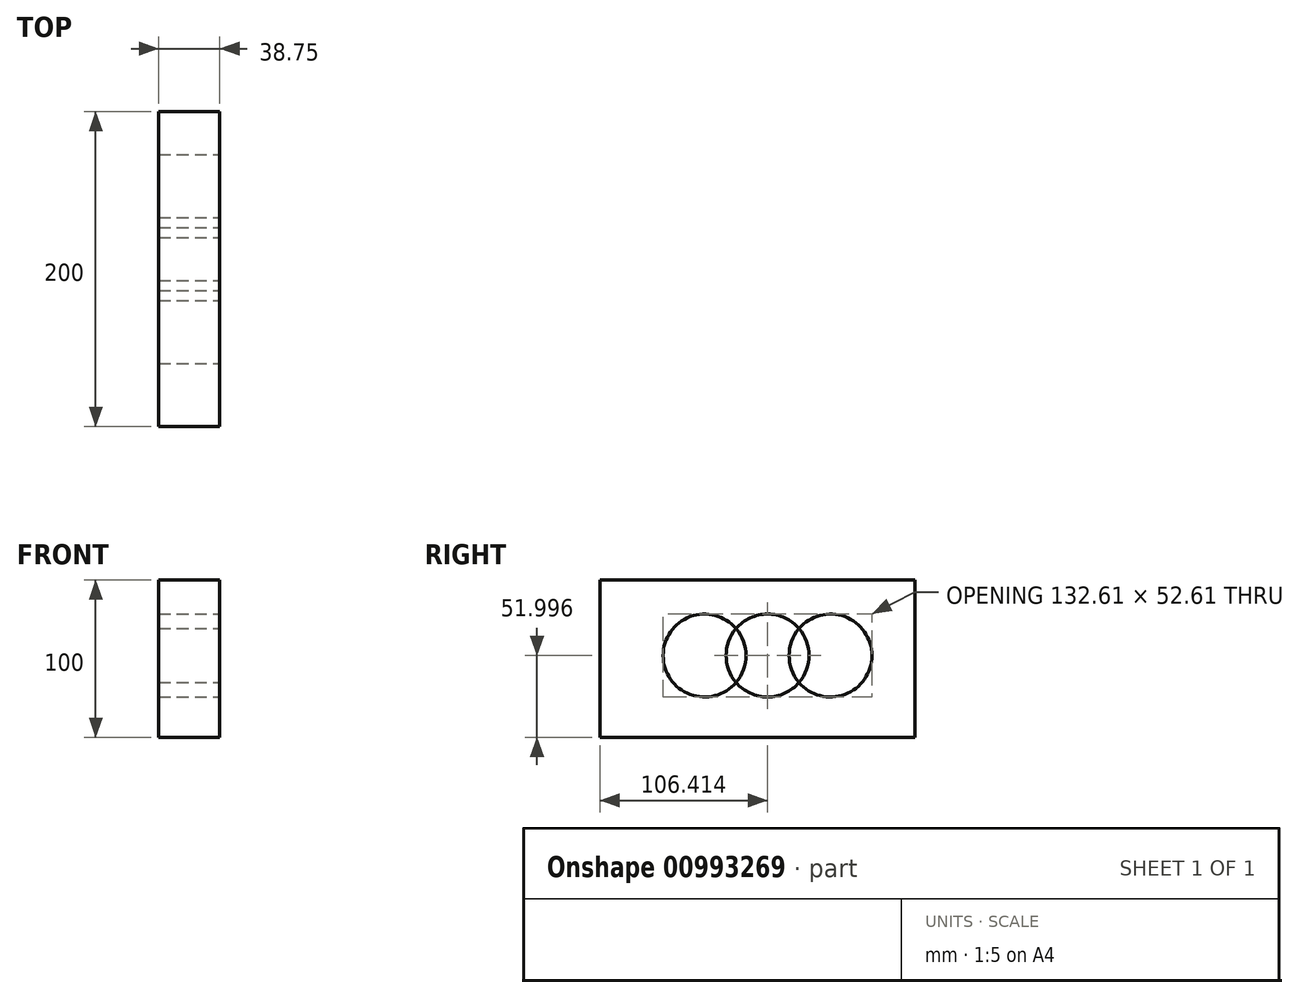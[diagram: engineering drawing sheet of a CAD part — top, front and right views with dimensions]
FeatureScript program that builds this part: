
annotation { "Feature Type Name" : "Feature", "Feature Type Description" : "" }
export const myFeature = defineFeature(function(context is Context, id is Id, definition is map)
    precondition{}
    {
        {
            var Q0;
            Q0=qCreatedBy(makeId("Top.planeOp"),FACE);
            var sketch = newSketch(context, id + "F0", { "sketchPlane" : qUnion([Q0])});
            skLineSegment(sketch, "E0", {"start": v(-54.4, 379.86) * mm, "end": v(-54.4, 179.86) * mm});
            skLineSegment(sketch, "E1", {"start": v(-54.4, 379.86) * mm, "end": v(-93.15, 379.86) * mm});
            skLineSegment(sketch, "E2", {"start": v(-93.15, 379.86) * mm, "end": v(-93.15, 179.86) * mm});
            skLineSegment(sketch, "E3", {"start": v(-93.15, 179.86) * mm, "end": v(-54.4, 179.86) * mm});
            skSolve(sketch);
        }
        {
            var Q0;
            Q0=makeQuery(id+"F0.imprint","IMPRINT",FACE,{"disambiguationData":[TD([[makeQuery(id+"F0.imprint","IMPRINT",EDGE,{"derivedFrom":sQuery(id+"F0.wireOp",EDGE,"E0")}),-1.0]])]});
            extrude(context, id + "F1", {"entities" : qUnion([Q0]), "depth" : 100 * mm, "offsetDistance" : 25 * mm});
        }
        {
            var Q0;
            Q0=makeQuery(id+"F1.opExtrude","SWEPT_FACE",FACE,{"disambiguationData":[OSD([sQuery(id+"F0.wireOp",EDGE,"E0")])]});
            var sketch = newSketch(context, id + "F2", { "sketchPlane" : qUnion([Q0])});
            skCircle(sketch, "E4", {"center": v(246.27, 52) * mm, "radius": 26.3 * mm});
            skCircle(sketch, "E5.1.0.0", {"center": v(286.27, 52) * mm, "radius": 26.3 * mm});
            skCircle(sketch, "E5.2.0.0", {"center": v(326.27, 52) * mm, "radius": 26.3 * mm});
            skLineSegment(sketch, "E5.direction1", {"start": v(246.27, 52) * mm, "end": v(286.27, 52) * mm, "construction": true});
            skSolve(sketch);
        }
        {
            var Q0;
            {var subQ0=sQuery(id+"F2.wireOp",EDGE,"E5.1.0.0");var subQ1=sQuery(id+"F2.wireOp",EDGE,"E4");var subQ2=makeQuery(id+"F2.imprint","INTERSECT",VERTEX,{"disambiguationData":[OD(0.0)],"derivedFrom":[subQ1,subQ0]});Q0=makeQuery(id+"F2.imprint","IMPRINT",FACE,{"disambiguationData":[TD([[makeQuery(id+"F2.imprint","IMPRINT",EDGE,{"disambiguationData":[TD([[subQ2,-1.0]])],"derivedFrom":subQ1}),1.0]])]});}
            var Q1;
            {var subQ0=sQuery(id+"F2.wireOp",EDGE,"E5.1.0.0");var subQ1=sQuery(id+"F2.wireOp",EDGE,"E4");var subQ2=makeQuery(id+"F2.imprint","INTERSECT",VERTEX,{"disambiguationData":[OD(0.0)],"derivedFrom":[subQ1,subQ0]});Q1=makeQuery(id+"F2.imprint","IMPRINT",FACE,{"disambiguationData":[TD([[makeQuery(id+"F2.imprint","IMPRINT",EDGE,{"disambiguationData":[TD([[subQ2,1.0]])],"derivedFrom":subQ1}),-1.0]])]});}
            var Q2;
            {var subQ0=sQuery(id+"F2.wireOp",EDGE,"E5.2.0.0");var subQ1=sQuery(id+"F2.wireOp",EDGE,"E5.1.0.0");var subQ2=makeQuery(id+"F2.imprint","INTERSECT",VERTEX,{"disambiguationData":[OD(0.0)],"derivedFrom":[subQ1,subQ0]});Q2=makeQuery(id+"F2.imprint","IMPRINT",FACE,{"disambiguationData":[TD([[makeQuery(id+"F2.imprint","IMPRINT",EDGE,{"disambiguationData":[TD([[subQ2,1.0]])],"derivedFrom":subQ1}),-1.0]])]});}
            extrude(context, id + "F3", {"entities" : qUnion([Q0, Q1, Q2]), "operationType" : NewBodyOperationType.REMOVE, "oppositeDirection" : true, "depth" : 200 * mm, "offsetDistance" : 25 * mm});
        }
    });
